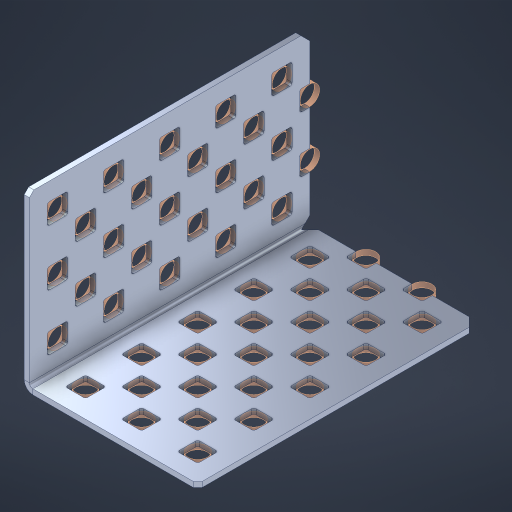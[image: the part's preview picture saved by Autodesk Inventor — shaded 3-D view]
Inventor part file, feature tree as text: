
AUTODESK INVENTOR PART (.ipt)
format: ipt  version: 2023 (Build 270158000, 158)  size: 856,576 bytes
history: native  units: in
note: dims shown in document units (in); Inventor stores cm internally (conversion verified against a paired STEP export)
features: other x56, extrude x48, sheet_metal_op x8, sketch x7, pattern_linear x3, mirror x1, chamfer x1
ambient origin geometry x8: Origin, YZ Plane, XZ Plane, XY Plane, X Axis, Y Axis, Z Axis, Center Point
bodies: Solid1 (feature_tree), Body (feature_tree)
feature tree (124):
  sheet_metal_op  "Flanges"
  sheet_metal_op  "Body Pattern"
  pattern_linear  "Center Double"  Spacing1=1.5in  [1 undecoded]
  pattern_linear  "Center Pattern"  Spacing1=0.1875in  [1 undecoded]
  other  "Arc Length"
  pattern_linear  "Notch Pattern"  Spacing1=0.0469in  [1 undecoded]
  other  "Diagonal Plane"
  mirror  "Everything Mirrored"
  chamfer  "End Chamfer"
  sketch  "Sketch1"  dims[d0=1.5in]
  other  "Plate1"
  sketch  "Sketch2"  dims[d1=2.5in]
  other  "Plate2"
  sheet_metal_op  "Bend1"
  sheet_metal_op  "Corner1"
  sketch  "Sketch8"  dims[d2=0.0469in]
  sketch  "Sketch9"  dims[d3=0.0469in]
  other  "Srf91"
  sheet_metal_op  "Body Pattern Sketch"
  other  "Srf92"
  sketch  "Sketch13"  dims[d4=0.0234in]
  sketch  "Sketch15"  dims[d5=0.0938in]
  sketch  "Sketch16"  dims[d6=0.0469in d7=1.5in d8=90.0deg d9=0.0312in d10=0.1875in d11=0.0469in d12=0.0469in d49=0.182in d50=0.02in d52=0.25in d53=0.0469in d54=0.0in d55=0.172in d56=1.0in d57=0.0in d85=0.1473in d86=0.1659in d89=0.0469in d90=0.0in d91=0.04in d92=0.0491in d95=2.5in d96=0.04in d97=0.25in d98=45.0deg d106=0.182in d107=0.02in d110=0.0469in d111=0.0in d112=0.172in d113=0.5in d114=0.0in d117=0.5in d126=0.0491in d127=0.1227in d128=0.08in d129=0.04in d130=2.5in d131=0.25in d132=1.9685in d134=0.5in d135=1.1811in d137=0.5in d140=0.5in d141=1.0in d142=0.3937in d144=0.5in d145=0.071in d146=0.7874in d148=0.5in]
  other  "Srf786"
  other  "Srf856"
  other  "Srf889"
  other  "Srf890"
  other  "Srf891"
  other  "Srf1275"
  other  "Srf1276"
  other  "Srf1278"
  other  "Srf1277"
  other  "Srf1285"
  other  "Srf1286"
  other  "Srf1287"
  other  "Srf1445"
  other  "Srf1537"
  other  "Srf2009"
  other  "Srf2010"
  other  "Srf2011"
  other  "Srf2012"
  other  "Srf2013"
  other  "Srf2043"
  other  "Srf2044"
  other  "Srf2045"
  other  "Srf2046"
  other  "Srf2076"
  other  "Srf2077"
  other  "Srf2078"
  other  "Srf2079"
  other  "Srf2080"
  other  "Srf2081"
  other  "Srf2082"
  other  "Srf2083"
  other  "Srf2084"
  other  "Srf2085"
  other  "Srf2086"
  other  "Srf2087"
  other  "Srf2088"
  other  "Srf2179"
  other  "Srf2180"
  other  "Srf2181"
  other  "Srf2182"
  other  "Srf2183"
  other  "Srf2184"
  other  "Srf2185"
  other  "Srf2186"
  other  "Srf2187"
  other  "Srf2188"
  other  "Srf2189"
  other  "Srf2190"
  sheet_metal_op  "Body Stamp"
  sheet_metal_op  "Body Circle"
  other  "Center Stamp"
  other  "Center Circle"
  sheet_metal_op  "Notch"
  extrude  "ExtrusionSrf92"  Depth=0.0469in
  extrude  "ExtrusionSrf856"  Depth=0.3937in
  extrude  "ExtrusionSrf889"  Depth=0.02in
  extrude  "ExtrusionSrf890"  Depth=0.25in
  extrude  "ExtrusionSrf891"  Depth=0.0469in
  extrude  "ExtrusionSrf1275"  TaperAngle=0.0deg  [1 undecoded]
  extrude  "ExtrusionSrf1276"  Depth=0.3937in
  extrude  "ExtrusionSrf1277"  Depth=0.3937in TaperAngle=0.0deg
  extrude  "ExtrusionSrf1345"  Depth=0.3937in
  extrude  "ExtrusionSrf1346"  Depth=0.3937in
  extrude  "ExtrusionSrf1347"  Depth=0.0469in
  extrude  "ExtrusionSrf1348"  Depth=0.3937in TaperAngle=0.0deg
  extrude  "ExtrusionSrf1445"  Depth=0.3937in
  extrude  "ExtrusionSrf1537"  Depth=0.25in TaperAngle=45.0deg
  extrude  "ExtrusionSrf2009"  Depth=0.3937in
  extrude  "ExtrusionSrf2010"  Depth=0.02in
  extrude  "ExtrusionSrf2011"  Depth=0.0469in
  extrude  "ExtrusionSrf2012"  TaperAngle=0.0deg  [1 undecoded]
  extrude  "ExtrusionSrf2013"  Depth=0.3937in
  extrude  "ExtrusionSrf2043"  Depth=0.3937in TaperAngle=0.0deg
  extrude  "ExtrusionSrf2044"  Depth=0.3937in
  extrude  "ExtrusionSrf2045"  Depth=0.3937in
  extrude  "ExtrusionSrf2046"  Depth=0.3937in
  extrude  "ExtrusionSrf2076"  Depth=0.3937in
  extrude  "ExtrusionSrf2077"  Depth=0.3937in
  extrude  "ExtrusionSrf2078"  Depth=0.3937in
  extrude  "ExtrusionSrf2079"  Depth=0.25in
  extrude  "ExtrusionSrf2080"  Depth=0.3937in
  extrude  "ExtrusionSrf2081"  Depth=0.3937in
  extrude  "ExtrusionSrf2082"  Depth=0.3937in
  extrude  "ExtrusionSrf2083"  Depth=0.3937in
  extrude  "ExtrusionSrf2084"  Depth=0.3937in
  extrude  "ExtrusionSrf2085"  Depth=0.3937in
  extrude  "ExtrusionSrf2086"  Depth=0.3937in
  extrude  "ExtrusionSrf2087"  [1 undecoded]
  extrude  "ExtrusionSrf2088"  [1 undecoded]
  extrude  "ExtrusionSrf2179"  [1 undecoded]
  extrude  "ExtrusionSrf2180"  [1 undecoded]
  extrude  "ExtrusionSrf2181"  [1 undecoded]
  extrude  "ExtrusionSrf2182"  [1 undecoded]
  extrude  "ExtrusionSrf2183"  [1 undecoded]
  extrude  "ExtrusionSrf2184"  [1 undecoded]
  extrude  "ExtrusionSrf2185"  [1 undecoded]
  extrude  "ExtrusionSrf2186"  [1 undecoded]
  extrude  "ExtrusionSrf2187"  [1 undecoded]
  extrude  "ExtrusionSrf2188"  [1 undecoded]
  extrude  "ExtrusionSrf2189"  [1 undecoded]
  extrude  "ExtrusionSrf2190"  [1 undecoded]
note: 19 required parameter values undecoded (feature->parameter linkage not recoverable at this tier; creation-order binding heuristic only, values carry confidence <= 0.55)
